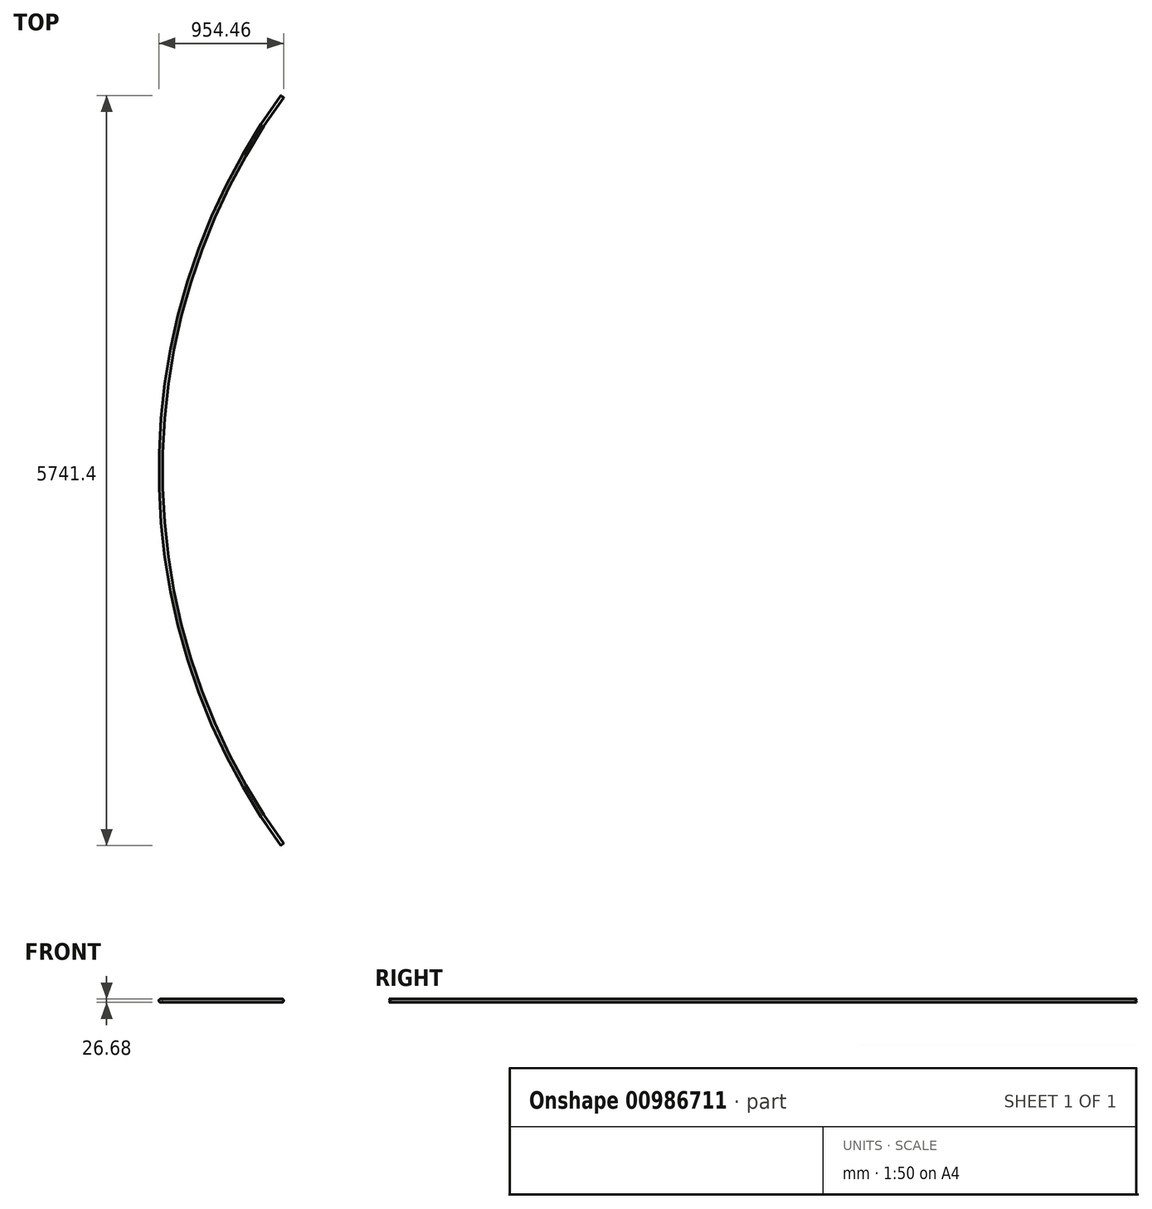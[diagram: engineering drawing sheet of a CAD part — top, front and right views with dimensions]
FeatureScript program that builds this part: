
annotation { "Feature Type Name" : "Feature", "Feature Type Description" : "" }
export const myFeature = defineFeature(function(context is Context, id is Id, definition is map)
    precondition{}
    {
        {
            var Q0;
            Q0=qCreatedBy(makeId("Front.planeOp"),FACE);
            var sketch = newSketch(context, id + "F0", { "sketchPlane" : qUnion([Q0])});
            skCircle(sketch, "E0", {"center": v(0, 0) * mm, "radius": 13.34 * mm});
            skCircle(sketch, "E1.0", {"center": v(0, 0) * mm, "radius": 11.23 * mm});
            skLineSegment(sketch, "E2", {"start": v(0, 0) * mm, "end": v(4870, 0) * mm, "construction": true});
            skLineSegment(sketch, "E3", {"start": v(4870, 0) * mm, "end": v(4870, -100) * mm, "construction": true});
            skSolve(sketch);
        }
        {
            var Q0;
            Q0=qSketchRegion(id+"F0",true);
            var Q1;
            Q1=sQuery(id+"F0.wireOp",EDGE,"E3");
            revolve(context, id + "F1", {"surfaceOperationType" : NewSurfaceOperationType.NEW, "entities" : qUnion([Q0]), "axis" : qUnion([Q1]), "revolveType" : RevolveType.SYMMETRIC, "angle" : 72.01 * degree});
        }
    });
